# Revit family: Hot-Water-Heater
name_source: partatom
category: Mechanical Equipment
units: mm (PartAtom-declared; Revit-internal decimal feet)

## family parameters
Always vertical = Yes
Classification Number = 23.75.10.11.14
Cut with Voids When Loaded = No
Maintain Annotation Orientation = No
Part Type = Normal
Room Calculation Point = No
Round Connector Dimension = Use Diameter
Shared = No
Work Plane-Based = Yes

## types (3) — shared parameters
Assembly Code = D3020100
Case Material = ARCAT - Metal - Aluminum, Painted - Tan
Construction Details = http://www.arcat.com
Default Elevation = 4' - 0"
Description = Tank Type Hot Water Heater
Duct Type = ARCAT - Metal - Aluminum
Expected Lifespan (Years) = 20
Fitting Material = ARCAT - Metal - Brass
Flue Diameter = 0' - 4"
Fuel Type = ARCAT - Fuel - Natural Gas
Green Building-LEED = http://www.arcat.com
Keynote = 15500
Maintenance Schedule (Months) = 12
Manufacturer = Generic
Manufacturer Fax = (203) 939-2444
Manufacturer Website = http://www.arcat.com
Model = Generic
Output Water Temperature = 140
Product Data = http://www.arcat.com
Product Properties = http://www.arcat.com
Recovery (G/Hr) = 90
Specification = http://www.arcat.com
Tank Capacity = 60
Type Comments = Hot Water Heater
Warranty Duration (Years) = 10
fluerad = 0' - 2"
risrheight = 0' - 5"

## per-type parameters (varying)
| type | BTU Input | Electric Heated | Element Wattage | Gas Fired | Indirect System | Input Water Temperature |
| Electric | 0 | Yes | 4500 | No | No | 0 |
| Gas Fired | 40000 | No | 0 | Yes | No | 0 |
| Indirect Heat | 0 | No | 0 | No | Yes | 160 |

## geometry (parser evidence)
native form markers: Sweep x3
no freeform markers — native parametric forms only
